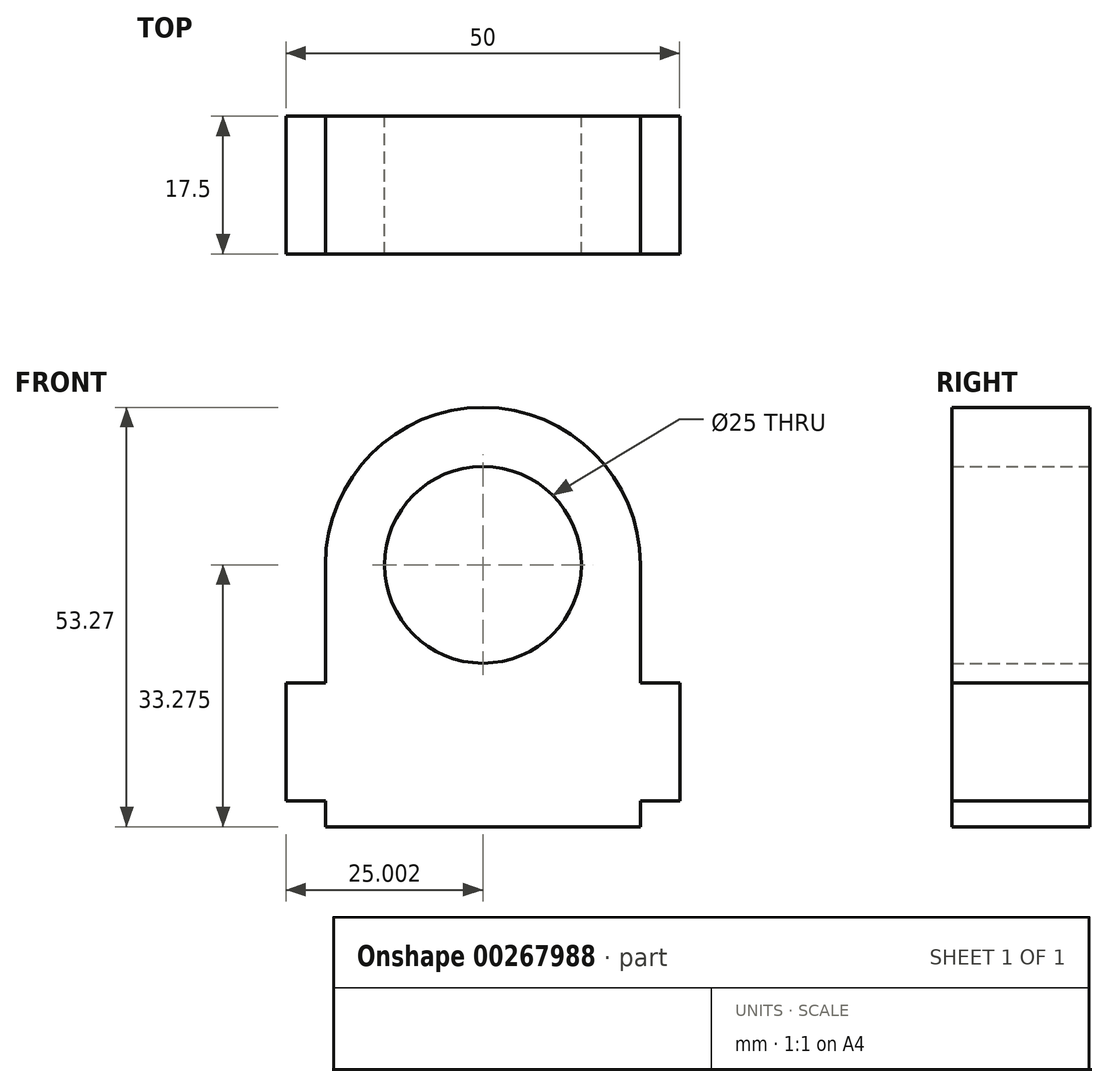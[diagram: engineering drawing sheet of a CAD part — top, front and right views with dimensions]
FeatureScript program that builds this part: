
annotation { "Feature Type Name" : "Feature", "Feature Type Description" : "" }
export const myFeature = defineFeature(function(context is Context, id is Id, definition is map)
    precondition{}
    {
        {
            var Q0;
            Q0=qCreatedBy(makeId("Front.planeOp"),FACE);
            var sketch = newSketch(context, id + "F0", { "sketchPlane" : qUnion([Q0])});
            skLineSegment(sketch, "E0", {"start": v(-5.04, 9.18) * mm, "end": v(-45.04, 9.18) * mm});
            skLineSegment(sketch, "E1", {"start": v(-45.04, 12.45) * mm, "end": v(-45.04, 9.18) * mm});
            skLineSegment(sketch, "E2", {"start": v(-45.04, 12.45) * mm, "end": v(-50.04, 12.45) * mm});
            skPoint(sketch, "E3.end.orphan", {"position": v(-5, 12.45) * mm});
            skLineSegment(sketch, "E4", {"start": v(-5.04, 12.45) * mm, "end": v(-5.04, 9.18) * mm});
            skLineSegment(sketch, "E5", {"start": v(-5.04, 12.45) * mm, "end": v(-0.04, 12.45) * mm});
            skLineSegment(sketch, "E6", {"start": v(-50.04, 12.45) * mm, "end": v(-50.04, 27.45) * mm});
            skLineSegment(sketch, "E7", {"start": v(-50.04, 27.45) * mm, "end": v(-45.04, 27.45) * mm});
            skLineSegment(sketch, "E8", {"start": v(-0.04, 12.45) * mm, "end": v(-0.04, 27.45) * mm});
            skLineSegment(sketch, "E9", {"start": v(-0.04, 27.45) * mm, "end": v(-5.04, 27.45) * mm});
            skLineSegment(sketch, "E10", {"start": v(-45.04, 27.45) * mm, "end": v(-45.04, 42.45) * mm});
            skLineSegment(sketch, "E11", {"start": v(-5.04, 27.45) * mm, "end": v(-5.04, 42.45) * mm});
            skArc(sketch, "E12", {"start": v(-5.04, 42.45) * mm, "mid": v(-25.04, 62.45) * mm, "end": v(-45.04, 42.45) * mm});
            skCircle(sketch, "E13", {"center": v(-25.04, 42.45) * mm, "radius": 12.5 * mm});
            skSolve(sketch);
        }
        {
            var Q0;
            Q0=makeQuery(id+"F0.imprint","IMPRINT",FACE,{"disambiguationData":[TD([[makeQuery(id+"F0.imprint","IMPRINT",EDGE,{"derivedFrom":sQuery(id+"F0.wireOp",EDGE,"E0")}),-1.0]])]});
            extrude(context, id + "F1", {"entities" : qUnion([Q0]), "depth" : 17.5 * mm});
        }
    });
